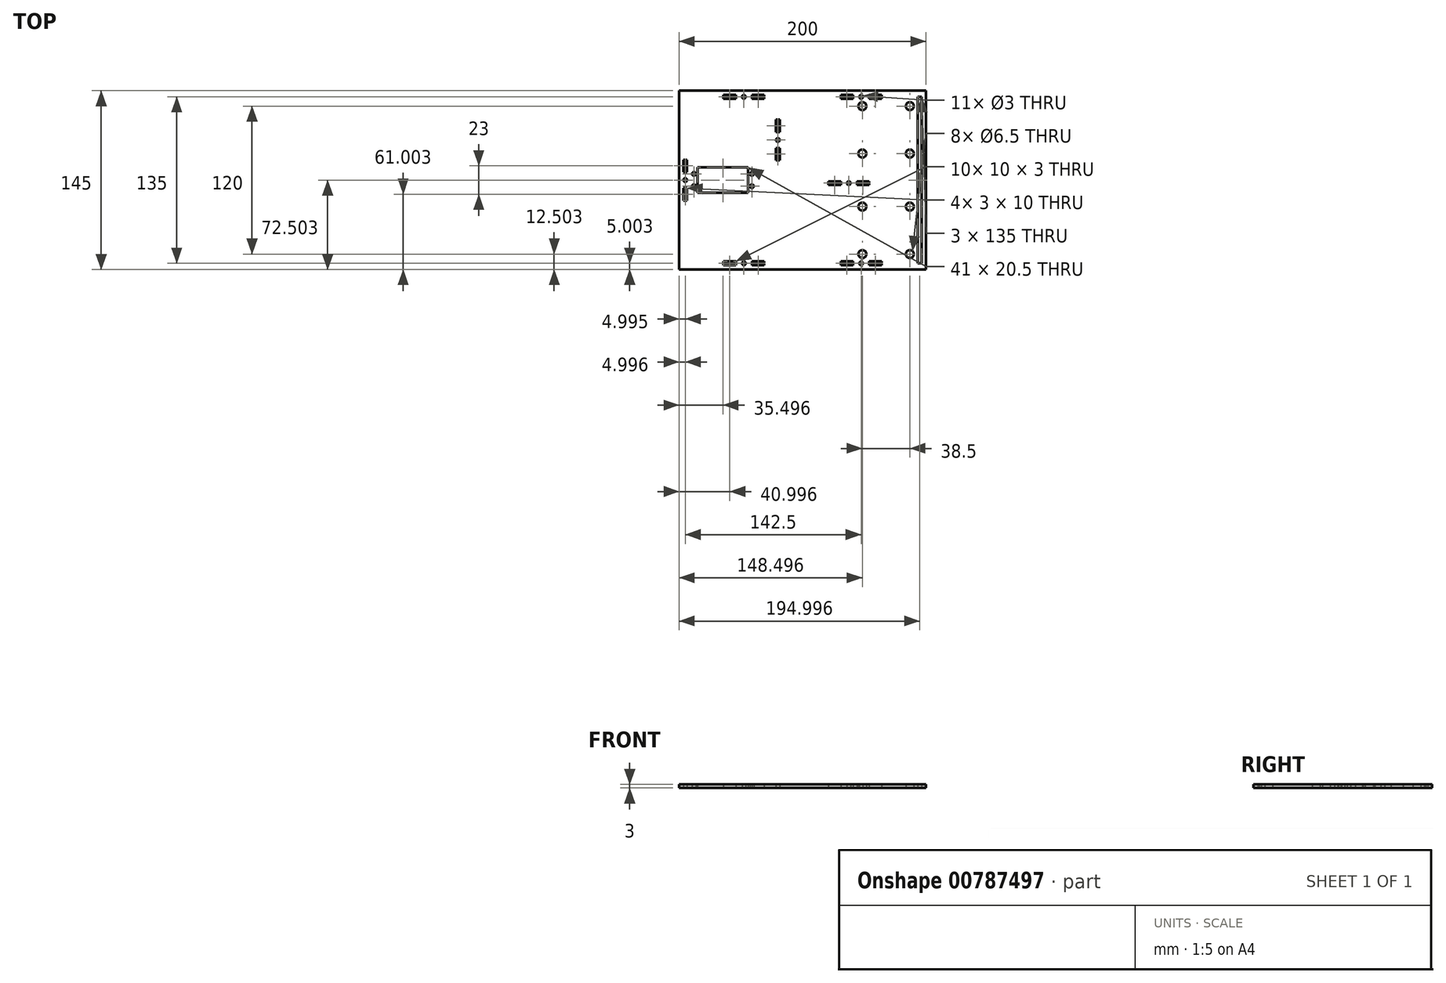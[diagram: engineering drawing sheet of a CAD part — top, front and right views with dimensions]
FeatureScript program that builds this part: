
annotation { "Feature Type Name" : "Feature", "Feature Type Description" : "" }
export const myFeature = defineFeature(function(context is Context, id is Id, definition is map)
    precondition{}
    {
        {
            var Q0;
            Q0=qCreatedBy(makeId("Top.planeOp"),FACE);
            var sketch = newSketch(context, id + "F0", { "sketchPlane" : qUnion([Q0])});
            skLineSegment(sketch, "E0.bottom", {"start": v(112.27, 154.56) * mm, "end": v(312.27, 154.56) * mm});
            skLineSegment(sketch, "E0.top", {"start": v(112.27, 9.56) * mm, "end": v(312.27, 9.56) * mm});
            skLineSegment(sketch, "E0.left", {"start": v(112.27, 154.56) * mm, "end": v(112.27, 9.56) * mm});
            skLineSegment(sketch, "E0.right", {"start": v(312.27, 154.56) * mm, "end": v(312.27, 9.56) * mm});
            skLineSegment(sketch, "E1.top", {"start": v(307.27, 79.56) * mm, "end": v(192.27, 79.56) * mm, "construction": true});
            skLineSegment(sketch, "E1.right", {"start": v(192.27, 149.56) * mm, "end": v(192.27, 79.56) * mm, "construction": true});
            skLineSegment(sketch, "E2.bottom", {"start": v(127.27, 92.31) * mm, "end": v(168.27, 92.31) * mm});
            skLineSegment(sketch, "E2.top", {"start": v(127.27, 71.81) * mm, "end": v(168.27, 71.81) * mm});
            skLineSegment(sketch, "E2.left", {"start": v(127.27, 92.31) * mm, "end": v(127.27, 71.81) * mm});
            skLineSegment(sketch, "E2.right", {"start": v(168.27, 92.31) * mm, "end": v(168.27, 71.81) * mm});
            skLineSegment(sketch, "E3", {"start": v(112.27, 82.06) * mm, "end": v(127.27, 82.06) * mm, "construction": true});
            skLineSegment(sketch, "E4.0", {"start": v(307.27, 149.56) * mm, "end": v(307.27, 14.56) * mm, "construction": true});
            skLineSegment(sketch, "E5.bottom", {"start": v(305.77, 149.56) * mm, "end": v(308.77, 149.56) * mm});
            skLineSegment(sketch, "E5.top", {"start": v(305.77, 14.56) * mm, "end": v(308.77, 14.56) * mm});
            skLineSegment(sketch, "E5.left", {"start": v(305.77, 149.56) * mm, "end": v(305.77, 14.56) * mm});
            skLineSegment(sketch, "E5.right", {"start": v(308.77, 149.56) * mm, "end": v(308.77, 14.56) * mm});
            skPoint(sketch, "E5.middle", {"position": v(307.27, 82.06) * mm});
            skLineSegment(sketch, "E6.0", {"start": v(117.27, 149.56) * mm, "end": v(315.63, 149.56) * mm, "construction": true});
            skLineSegment(sketch, "E7.0", {"start": v(117.27, 149.56) * mm, "end": v(117.27, 14.56) * mm, "construction": true});
            skLineSegment(sketch, "E8.0", {"start": v(117.27, 14.56) * mm, "end": v(308.77, 14.56) * mm, "construction": true});
            skCircle(sketch, "E9", {"center": v(259.77, 149.56) * mm, "radius": 1.5 * mm});
            skCircle(sketch, "E10", {"center": v(164.77, 149.56) * mm, "radius": 1.5 * mm});
            skPoint(sketch, "E11", {"position": v(117.27, 149.56) * mm});
            skLineSegment(sketch, "E12.bottom", {"start": v(148.27, 151.06) * mm, "end": v(158.27, 151.06) * mm});
            skLineSegment(sketch, "E12.top", {"start": v(148.27, 148.06) * mm, "end": v(158.27, 148.06) * mm});
            skLineSegment(sketch, "E12.left", {"start": v(148.27, 151.06) * mm, "end": v(148.27, 148.06) * mm});
            skLineSegment(sketch, "E12.right", {"start": v(158.27, 151.06) * mm, "end": v(158.27, 148.06) * mm});
            skPoint(sketch, "E12.middle", {"position": v(153.27, 149.56) * mm});
            skLineSegment(sketch, "E13.bottom", {"start": v(171.27, 151.06) * mm, "end": v(181.27, 151.06) * mm});
            skLineSegment(sketch, "E13.top", {"start": v(171.27, 148.06) * mm, "end": v(181.27, 148.06) * mm});
            skLineSegment(sketch, "E13.left", {"start": v(171.27, 151.06) * mm, "end": v(171.27, 148.06) * mm});
            skLineSegment(sketch, "E13.right", {"start": v(181.27, 151.06) * mm, "end": v(181.27, 148.06) * mm});
            skPoint(sketch, "E13.middle", {"position": v(176.27, 149.56) * mm});
            skLineSegment(sketch, "E14.bottom", {"start": v(243.27, 151.06) * mm, "end": v(253.27, 151.06) * mm});
            skLineSegment(sketch, "E14.top", {"start": v(243.27, 148.06) * mm, "end": v(253.27, 148.06) * mm});
            skLineSegment(sketch, "E14.left", {"start": v(243.27, 151.06) * mm, "end": v(243.27, 148.06) * mm});
            skLineSegment(sketch, "E14.right", {"start": v(253.27, 151.06) * mm, "end": v(253.27, 148.06) * mm});
            skPoint(sketch, "E14.middle", {"position": v(248.27, 149.56) * mm});
            skLineSegment(sketch, "E15.bottom", {"start": v(266.27, 151.06) * mm, "end": v(276.27, 151.06) * mm});
            skLineSegment(sketch, "E15.top", {"start": v(266.27, 148.06) * mm, "end": v(276.27, 148.06) * mm});
            skLineSegment(sketch, "E15.left", {"start": v(266.27, 151.06) * mm, "end": v(266.27, 148.06) * mm});
            skLineSegment(sketch, "E15.right", {"start": v(276.27, 151.06) * mm, "end": v(276.27, 148.06) * mm});
            skPoint(sketch, "E15.middle", {"position": v(271.27, 149.56) * mm});
            skLineSegment(sketch, "E16.MirrorCS", {"start": v(181.27, 13.06) * mm, "end": v(181.27, 16.06) * mm});
            skLineSegment(sketch, "E17.MirrorCS", {"start": v(148.27, 13.06) * mm, "end": v(158.27, 13.06) * mm});
            skLineSegment(sketch, "E18.MirrorCS", {"start": v(148.27, 16.06) * mm, "end": v(158.27, 16.06) * mm});
            skLineSegment(sketch, "E19.MirrorCS", {"start": v(171.27, 13.06) * mm, "end": v(181.27, 13.06) * mm});
            skLineSegment(sketch, "E20.MirrorCS", {"start": v(148.27, 13.06) * mm, "end": v(148.27, 16.06) * mm});
            skLineSegment(sketch, "E21.MirrorCS", {"start": v(171.27, 16.06) * mm, "end": v(181.27, 16.06) * mm});
            skCircle(sketch, "E22.MirrorC", {"center": v(164.77, 14.56) * mm, "radius": 1.5 * mm});
            skPoint(sketch, "E23.MirrorP", {"position": v(153.27, 14.56) * mm});
            skLineSegment(sketch, "E24.MirrorCS", {"start": v(158.27, 13.06) * mm, "end": v(158.27, 16.06) * mm});
            skLineSegment(sketch, "E25.MirrorCS", {"start": v(171.27, 13.06) * mm, "end": v(171.27, 16.06) * mm});
            skPoint(sketch, "E26.MirrorP", {"position": v(176.27, 14.56) * mm});
            skLineSegment(sketch, "E27.MirrorCS", {"start": v(276.27, 13.06) * mm, "end": v(276.27, 16.06) * mm});
            skLineSegment(sketch, "E28.MirrorCS", {"start": v(253.27, 13.06) * mm, "end": v(253.27, 16.06) * mm});
            skLineSegment(sketch, "E29.MirrorCS", {"start": v(266.27, 13.06) * mm, "end": v(266.27, 16.06) * mm});
            skLineSegment(sketch, "E30.MirrorCS", {"start": v(243.27, 13.06) * mm, "end": v(243.27, 16.06) * mm});
            skPoint(sketch, "E31.MirrorP", {"position": v(271.27, 14.56) * mm});
            skCircle(sketch, "E32.MirrorC", {"center": v(259.77, 14.56) * mm, "radius": 1.5 * mm});
            skLineSegment(sketch, "E33.MirrorCS", {"start": v(243.27, 16.06) * mm, "end": v(253.27, 16.06) * mm});
            skLineSegment(sketch, "E34.MirrorCS", {"start": v(266.27, 16.06) * mm, "end": v(276.27, 16.06) * mm});
            skPoint(sketch, "E35.MirrorP", {"position": v(248.27, 14.56) * mm});
            skLineSegment(sketch, "E36.MirrorCS", {"start": v(243.27, 13.06) * mm, "end": v(253.27, 13.06) * mm});
            skLineSegment(sketch, "E37.MirrorCS", {"start": v(266.27, 13.06) * mm, "end": v(276.27, 13.06) * mm});
            skLineSegment(sketch, "E38.0.1.0", {"start": v(193.76, 131.06) * mm, "end": v(193.76, 121.06) * mm});
            skLineSegment(sketch, "E38.0.1.1", {"start": v(190.76, 131.06) * mm, "end": v(193.76, 131.06) * mm});
            skLineSegment(sketch, "E38.0.1.2", {"start": v(190.76, 131.06) * mm, "end": v(190.76, 121.06) * mm});
            skLineSegment(sketch, "E38.0.1.3", {"start": v(190.76, 121.06) * mm, "end": v(193.76, 121.06) * mm});
            skCircle(sketch, "E38.0.1.4", {"center": v(192.27, 114.56) * mm, "radius": 1.5 * mm});
            skLineSegment(sketch, "E38.0.1.5", {"start": v(190.76, 108.06) * mm, "end": v(193.76, 108.06) * mm});
            skLineSegment(sketch, "E38.0.1.6", {"start": v(193.76, 108.06) * mm, "end": v(193.76, 98.06) * mm});
            skLineSegment(sketch, "E38.0.1.7", {"start": v(190.76, 98.06) * mm, "end": v(193.76, 98.06) * mm});
            skLineSegment(sketch, "E38.0.1.8", {"start": v(190.76, 108.06) * mm, "end": v(190.76, 98.06) * mm});
            skLineSegment(sketch, "E38.0.2.0", {"start": v(233.27, 81.06) * mm, "end": v(243.27, 81.06) * mm});
            skLineSegment(sketch, "E38.0.2.1", {"start": v(233.27, 78.06) * mm, "end": v(233.27, 81.06) * mm});
            skLineSegment(sketch, "E38.0.2.2", {"start": v(233.27, 78.06) * mm, "end": v(243.27, 78.06) * mm});
            skLineSegment(sketch, "E38.0.2.3", {"start": v(243.27, 78.06) * mm, "end": v(243.27, 81.06) * mm});
            skCircle(sketch, "E38.0.2.4", {"center": v(249.77, 79.56) * mm, "radius": 1.5 * mm});
            skLineSegment(sketch, "E38.0.2.5", {"start": v(256.27, 78.06) * mm, "end": v(256.27, 81.06) * mm});
            skLineSegment(sketch, "E38.0.2.6", {"start": v(256.27, 81.06) * mm, "end": v(266.27, 81.06) * mm});
            skLineSegment(sketch, "E38.0.2.7", {"start": v(266.27, 78.06) * mm, "end": v(266.27, 81.06) * mm});
            skLineSegment(sketch, "E38.0.2.8", {"start": v(256.27, 78.06) * mm, "end": v(266.27, 78.06) * mm});
            skLineSegment(sketch, "E39.0.1.0", {"start": v(118.76, 98.56) * mm, "end": v(118.76, 88.56) * mm});
            skLineSegment(sketch, "E39.0.1.1", {"start": v(115.76, 98.56) * mm, "end": v(118.76, 98.56) * mm});
            skLineSegment(sketch, "E39.0.1.2", {"start": v(115.76, 98.56) * mm, "end": v(115.76, 88.56) * mm});
            skLineSegment(sketch, "E39.0.1.3", {"start": v(115.76, 88.56) * mm, "end": v(118.76, 88.56) * mm});
            skCircle(sketch, "E39.0.1.4", {"center": v(117.27, 82.06) * mm, "radius": 1.5 * mm});
            skLineSegment(sketch, "E39.0.1.5", {"start": v(115.76, 75.56) * mm, "end": v(118.76, 75.56) * mm});
            skLineSegment(sketch, "E39.0.1.6", {"start": v(118.76, 75.56) * mm, "end": v(118.76, 65.56) * mm});
            skLineSegment(sketch, "E39.0.1.7", {"start": v(115.76, 65.56) * mm, "end": v(118.76, 65.56) * mm});
            skLineSegment(sketch, "E39.0.1.8", {"start": v(115.76, 75.56) * mm, "end": v(115.76, 65.56) * mm});
            skLineSegment(sketch, "E40.0", {"start": v(171.27, 84.81) * mm, "end": v(171.27, 64.31) * mm, "construction": true});
            skLineSegment(sketch, "E41.0", {"start": v(124.27, 84.81) * mm, "end": v(124.27, 64.31) * mm, "construction": true});
            skLineSegment(sketch, "E42.0", {"start": v(112.26, 77.06) * mm, "end": v(127.26, 77.06) * mm, "construction": true});
            skLineSegment(sketch, "E43.0", {"start": v(112.26, 87.06) * mm, "end": v(127.26, 87.06) * mm, "construction": true});
            skCircle(sketch, "E44", {"center": v(124.27, 87.06) * mm, "radius": 1.5 * mm});
            skCircle(sketch, "E45", {"center": v(124.27, 77.06) * mm, "radius": 1.5 * mm});
            skLineSegment(sketch, "E46", {"start": v(168.27, 82.06) * mm, "end": v(176.34, 82.06) * mm, "construction": true});
            skCircle(sketch, "E47", {"center": v(171.27, 87.06) * mm, "radius": 1.5 * mm});
            skCircle(sketch, "E48", {"center": v(171.27, 77.06) * mm, "radius": 1.5 * mm});
            skLineSegment(sketch, "E49", {"start": v(312.27, 82.06) * mm, "end": v(484.51, 82.06) * mm, "construction": true});
            skLineSegment(sketch, "E50", {"start": v(484.51, 82.06) * mm, "end": v(516.51, 82.06) * mm, "construction": true});
            skLineSegment(sketch, "E51.0", {"start": v(484.51, 110.06) * mm, "end": v(516.51, 110.06) * mm, "construction": true});
            skLineSegment(sketch, "E52.0", {"start": v(484.51, 142.06) * mm, "end": v(516.51, 142.06) * mm, "construction": true});
            skCircle(sketch, "E53", {"center": v(299.27, 142.06) * mm, "radius": 3.25 * mm});
            skCircle(sketch, "E54", {"center": v(260.77, 142.06) * mm, "radius": 3.25 * mm});
            skCircle(sketch, "E55", {"center": v(260.77, 103.56) * mm, "radius": 3.25 * mm});
            skCircle(sketch, "E56", {"center": v(299.27, 103.56) * mm, "radius": 3.25 * mm});
            skLineSegment(sketch, "E57", {"start": v(516.51, 82.06) * mm, "end": v(524.51, 82.06) * mm, "construction": true});
            skCircle(sketch, "E58.MirrorC", {"center": v(299.27, 22.06) * mm, "radius": 3.25 * mm});
            skCircle(sketch, "E59.MirrorC", {"center": v(299.27, 60.56) * mm, "radius": 3.25 * mm});
            skCircle(sketch, "E60.MirrorC", {"center": v(260.77, 60.56) * mm, "radius": 3.25 * mm});
            skCircle(sketch, "E61.MirrorC", {"center": v(260.77, 22.06) * mm, "radius": 3.25 * mm});
            skSolve(sketch);
        }
        {
            var Q0;
            Q0=makeQuery(id+"F0.imprint","IMPRINT",FACE,{"disambiguationData":[TD([[makeQuery(id+"F0.imprint","IMPRINT",EDGE,{"derivedFrom":sQuery(id+"F0.wireOp",EDGE,"E0.bottom")}),-1.0]])]});
            extrude(context, id + "F1", {"entities" : qUnion([Q0]), "depth" : 3 * mm, "offsetDistance" : 25.4 * mm});
        }
    });
